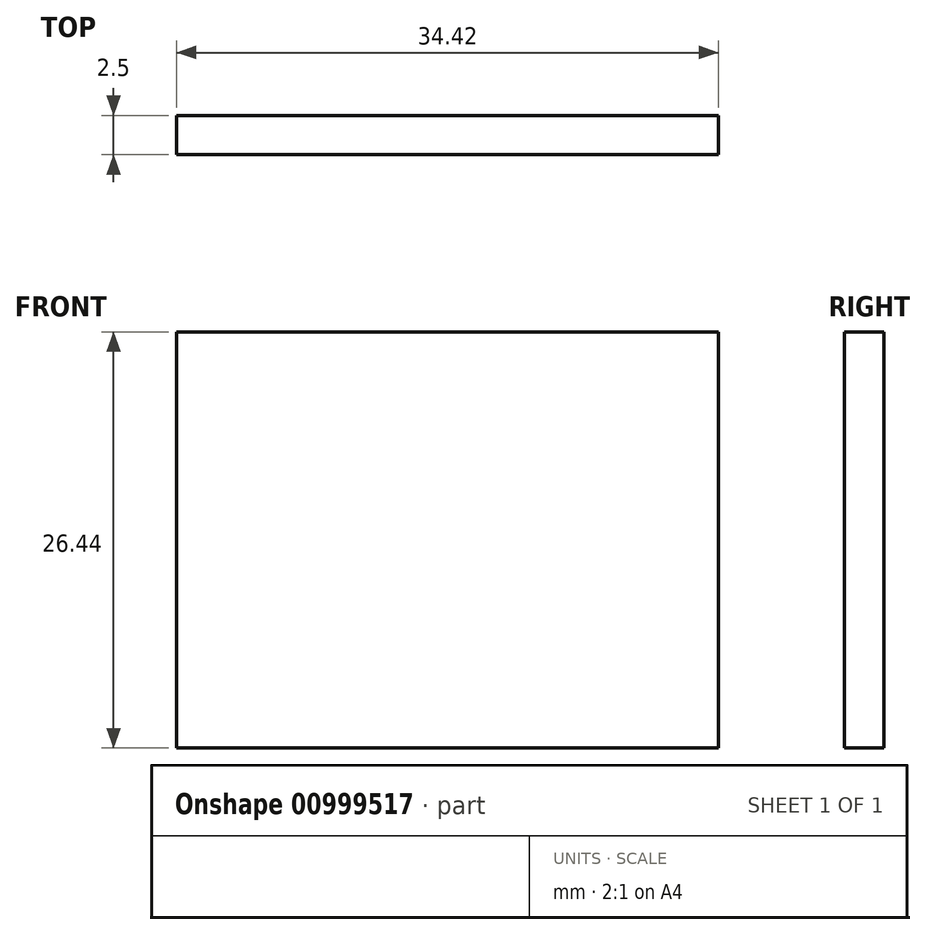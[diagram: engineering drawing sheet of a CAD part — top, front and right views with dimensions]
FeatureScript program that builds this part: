
annotation { "Feature Type Name" : "Feature", "Feature Type Description" : "" }
export const myFeature = defineFeature(function(context is Context, id is Id, definition is map)
    precondition{}
    {
        {
            var Q0;
            Q0=qCreatedBy(makeId("Front.planeOp"),FACE);
            var sketch = newSketch(context, id + "F0", { "sketchPlane" : qUnion([Q0])});
            skLineSegment(sketch, "E0", {"start": v(0, 0) * mm, "end": v(0, 26.44) * mm});
            skLineSegment(sketch, "E1", {"start": v(0, 26.44) * mm, "end": v(-34.42, 26.44) * mm});
            skLineSegment(sketch, "E2", {"start": v(-34.42, 26.44) * mm, "end": v(-34.42, 0) * mm});
            skLineSegment(sketch, "E3", {"start": v(-34.42, 0) * mm, "end": v(0, 0) * mm});
            skSolve(sketch);
        }
        {
            var Q0;
            Q0 = qSketchRegion(id + "F0", true);
            extrude(context, id + "F1", {"entities" : qUnion([Q0]), "depth" : 2.5 * mm, "offsetDistance" : 25.4 * mm});
        }
    });
